# Revit family: SIMES_S.3150W_Trim Applique
name_source: partatom
category: Lighting Fixtures
revit_build: Autodesk Revit 2016 (Build: 20150714_1515(x64)
units: mm (PartAtom-declared; Revit-internal decimal feet)

## family parameters
Cut with Voids When Loaded = No
Host = Face
Light Source = Yes
OmniClass Number = 23.80.70.14
OmniClass Title = Luminaries for External Lighting
Part Type = Normal
Room Calculation Point = No
Round Connector Dimension = Use Diameter
Shared = No

## types (1)
- SIMES_S.3150W_Trim Applique
    Approval mark = CE, ENEC
    Assembly Code = D5020
    BIMobject category = Outside
    Brand url = http://www.simes.it
    Color Filter = 16777215
    Color Rendering Index = CRI 90
    Colour Temperature = 3000
    Control Gear = electronic transformer
    Default Elevation = 1219 mm
    Description = TRIM SQUARE 170 APPLIQUE
Art. S.3150W
MODULES LED 3000K  230V CRI 90 MacAdam step 3
Rated luminaire luminous flux: 603lm
Rated input power: 9W
Luminaire efficacy: 67lm/W
Electronic ballast 220÷230V 50/60Hz
CE - ENEC 03

PRODUCT TYPE
Wall mounted luminaire. Bollard fitting ( bollard version ). IP rating IP 54
MATERIAL CHARACTERISTICS
Aluminium die cast housing in EN AB-47100 (low copper content) with high resistance against corrosion. Extruded EN AW-6060 aluminium structure (bollard version) with high corrosion resistance. Stone wash surface treatment prior to painting process. A4 grade Stainless Steel screws with 2,5-3% molybdenum content which increases the resistance against corrosion. Silicone gaskets. Painting Process : 3 Step Process
1) Surface treatment with BONDERITE. A heavy metal free chemical surface treatment containing ceramic nano particles giving a cohesive, inorganic and highly dense protective coating. 2) PRE POLYMERIZATION a process of introducing an epoxy primer with excellent characteristics to the paint which also offers very high resistance to oxidation due to its Zinc content. 3) POLYMERIZATION a process with the application of polyester powder with high resistance against UV rays and harsh weather conditions. Resistance test protection for Marine applications for 1200h.  Mechanical resistance IK 09
LIGHTING PERFORMANCE
Toughened glass diffuser 4mm thick. LOR --. Trim double emission has been developed to ensure maximum visual comfort. The direct light of the front side is diffused by a special glass, to prevents glare and avoid the visibility of the LEDs. The indirect light is evenly distributed on the wall thanks to a second diffusing glass positioned on the rear side of the luminaire. Colour rendering index  CRI 90, Colour stability step  MacAdam step 3. 
WIRING
Hard wired with H07RN-F cable 1,0m. Isolation: CLASS I . Available colours: White (cod.01), Aluminium grey (cod.14). Weight: 0.6 Kg Glow Wire test: --
Lamp included.
TRIM REGISTERED DESIGN
This luminaire contains built-in LED modules with energy class: A, A+, A++. In case of damage or malfunction please contact the manufacturer to receive additional instructions on how to replace and relative spare parts to order. The LED modules cannot be handled in the luminaire by the end user (Regulation UE 874/2012).
LED circuit boards are engineered accordingly to actual Lumen Maintenance regulation (LM80) and Technical Memorandum (TM21) where uniformity and quality of light is 50.000 hours referred to L70  B20 Ta 25°C.Lifecycle refers to LED circuit boards only, all others components of the luminaire are excluded.
    Design country = Italy
    Dimming Lamp Color Temperature Shift = <None>
    Edition number = 1
    Frequency = 50/60Hz
    IFC Classification = Light Fixture
    IK Rating = IK 06
    Installation instructions = http://www.simes.it
    Lamp = LED
    Lamp Light Flux = 900
    Lamp count = 1
    Last Update = 08/11/2018 17:17:51
    Lifetime = 50000 L70 B20 Ta 25°C
    Light Output Ratio = 100
    Luminous efficacy = 67
    Manufacturer = SIMES
    Manufacturer country = Italy
    Manufacturer name = Simes
    Masterformat 2014 Code = 26 56 00
    Masterformat 2014 Description = Exterior Lighting
    Material main = Aluminium
    Material secondary = Glass
    Model = S.3150W
    Mounting Place = Wall
    Mounting Type = Surface mounted
    NBS Reference Code = 49
    NBS Reference Description = Luminaries And Lamps
    Nominal height = 17000
    Nominal width = 17000
    OmniClass Code = 23-35 47 11
    OmniClass Description = Lighting Fixture
    Photometric Web File = S3150W.ies
    Product Group = wall-mounted luminaire
    Product Guid = 5eed9a8a-40da-4078-8ecc-114165e49aca
    Product Name = Trim Applique
    Product SKU = TRIM
    Product certification = http://www.simes.it
    Product data url = https://bimobject.com
    Product url = http://www.simes.it
    Protection Class = Protection class I
    Protection Degree = IP 54
    QR code = http://bimobject.com
    System Light Flux = 603
    System Power = 9
    Technical description = http://www.simes.it
    Tilt Angle = 90.00°
    Type Comments = SIMES S.p.A. - All rights reserved
    Type Image = trim-applique-170.jpg
    UNSPSC Code = 3911
    URL = http://www.simes.it
    Uniclass 1.4 Code = YJ73
    Uniclass 1.4 Description = Luminaries and lamps
    Uniclass 2.0 Code = PR-49
    Uniclass 2.0 Description = Luminaries and lamps
    Uniclass 2015 Code = EF_70_80
    Uniclass 2015 Name = Lighting
    Uniformat II Code = D5020
    Uniformat II Description = Lighting & Branch Wiring
    Voltage = 220÷230V
    Weight Net (Kg) = 1

## geometry (parser evidence)
native form markers: Blend x2, Sweep x2
no freeform markers — native parametric forms only
